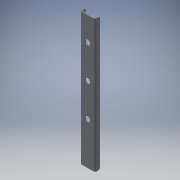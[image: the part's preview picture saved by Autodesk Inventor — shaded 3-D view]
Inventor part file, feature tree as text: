
AUTODESK INVENTOR PART (.ipt)
format: ipt  version: 2016 (Build 200138000, 138)  size: 153,600 bytes
history: native  units: mm
features: sheet_metal_op x2, sketch x2, extrude x1, pattern_linear x1, chamfer x1, other x1
ambient origin geometry x8: Origin, YZ Plane, XZ Plane, XY Plane, X Axis, Y Axis, Z Axis, Center Point
bodies: Solid1 (feature_tree)
feature tree (8):
  sheet_metal_op  "Contour Flange1"
  extrude  "Extrusion1"  Depth=50.0mm
  pattern_linear  "Rectangular Pattern1"  Spacing1=3.0mm  [1 undecoded]
  chamfer  "Corner Round1"
  sketch  "Sketch1"  dims[d0=15.0mm d1=50.0mm]
  other  "Plate1"
  sheet_metal_op  "Bend1"
  sketch  "Sketch2"  dims[d2=15.0mm d3=3.0mm d4=1.5mm d5=6.0mm d6=3.0mm d8=3.0mm d9=0.5mm d10=12.0mm d11=3.0mm d12=3.0mm d13=90.0mm d15=22.0mm d16=10.0mm d17=0.0mm d21=6.0mm]
note: 1 required parameter value undecoded (feature->parameter linkage not recoverable at this tier; creation-order binding heuristic only, values carry confidence <= 0.55)
